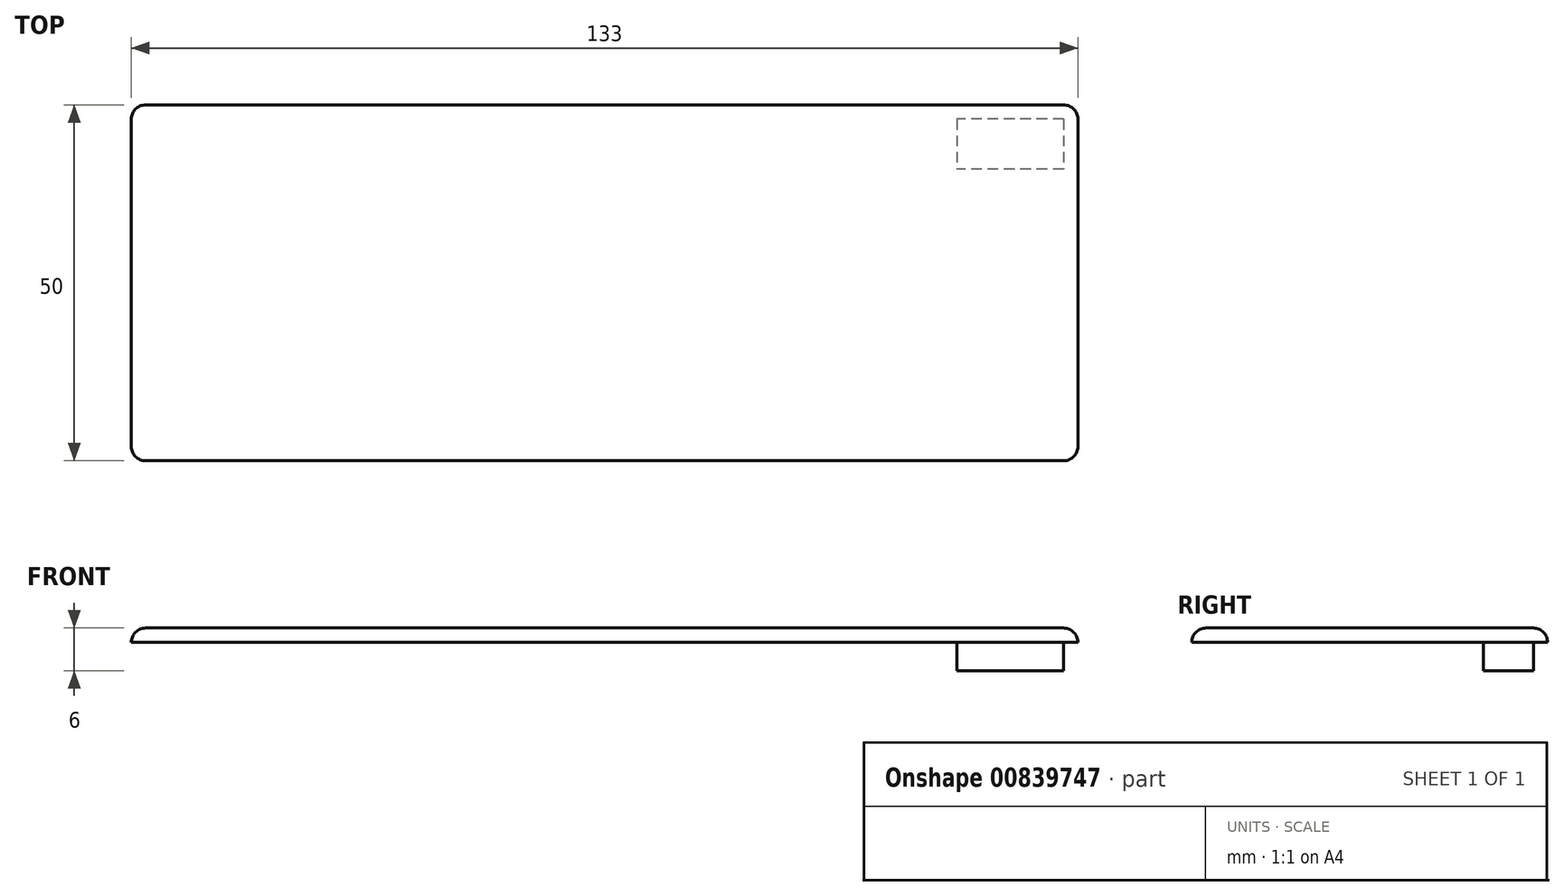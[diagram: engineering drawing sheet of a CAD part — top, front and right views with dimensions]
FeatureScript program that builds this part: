
annotation { "Feature Type Name" : "Feature", "Feature Type Description" : "" }
export const myFeature = defineFeature(function(context is Context, id is Id, definition is map)
    precondition{}
    {
        {
            var Q0;
            Q0=qCreatedBy(makeId("Top.planeOp"),FACE);
            var sketch = newSketch(context, id + "F0", { "sketchPlane" : qUnion([Q0])});
            skLineSegment(sketch, "E0.bottom", {"start": v(66.5, 25) * mm, "end": v(-66.5, 25) * mm});
            skLineSegment(sketch, "E0.top", {"start": v(66.5, -25) * mm, "end": v(-66.5, -25) * mm});
            skLineSegment(sketch, "E0.left", {"start": v(66.5, 25) * mm, "end": v(66.5, -25) * mm});
            skLineSegment(sketch, "E0.right", {"start": v(-66.5, 25) * mm, "end": v(-66.5, -25) * mm});
            skPoint(sketch, "E0.middle", {"position": v(0, 0) * mm});
            skSolve(sketch);
        }
        {
            var Q0;
            Q0=makeQuery(id+"F0.imprint","IMPRINT",FACE,{"disambiguationData":[TD([[makeQuery(id+"F0.imprint","IMPRINT",EDGE,{"derivedFrom":sQuery(id+"F0.wireOp",EDGE,"E0.bottom")}),1.0]])]});
            extrude(context, id + "F1", {"entities" : qUnion([Q0]), "depth" : 2 * mm, "offsetDistance" : 25 * mm});
        }
        {
            var Q0;
            Q0=makeQuery(id+"F1.opExtrude","CAP_FACE",FACE,{"disambiguationData":[OSD([sQuery(id+"F0.wireOp",EDGE,"E0.bottom"),sQuery(id+"F0.wireOp",EDGE,"E0.top"),sQuery(id+"F0.wireOp",EDGE,"E0.left"),sQuery(id+"F0.wireOp",EDGE,"E0.right")])],"isStart":true});
            var sketch = newSketch(context, id + "F2", { "sketchPlane" : qUnion([Q0])});
            skLineSegment(sketch, "E1.bottom", {"start": v(64.5, -23) * mm, "end": v(49.5, -23) * mm});
            skLineSegment(sketch, "E1.top", {"start": v(64.5, -16) * mm, "end": v(49.5, -16) * mm});
            skLineSegment(sketch, "E1.left", {"start": v(64.5, -23) * mm, "end": v(64.5, -16) * mm});
            skLineSegment(sketch, "E1.right", {"start": v(49.5, -23) * mm, "end": v(49.5, -16) * mm});
            skSolve(sketch);
        }
        {
            var Q0;
            Q0 = qSketchRegion(id + "F2", true);
            extrude(context, id + "F3", {"entities" : qUnion([Q0]), "operationType" : NewBodyOperationType.ADD, "depth" : 4 * mm, "offsetDistance" : 25 * mm});
        }
        {
            var Q0;
            Q0=makeQuery(id+"F1.opExtrude","SWEPT_EDGE",EDGE,{"disambiguationData":[OSD([sQuery(id+"F0.wireOp",EDGE,"E0.bottom"),sQuery(id+"F0.wireOp",EDGE,"E0.left")])]});
            var Q1;
            Q1=makeQuery(id+"F1.opExtrude","SWEPT_EDGE",EDGE,{"disambiguationData":[OSD([sQuery(id+"F0.wireOp",EDGE,"E0.top"),sQuery(id+"F0.wireOp",EDGE,"E0.left")])]});
            var Q2;
            Q2=makeQuery(id+"F1.opExtrude","SWEPT_EDGE",EDGE,{"disambiguationData":[OSD([sQuery(id+"F0.wireOp",EDGE,"E0.bottom"),sQuery(id+"F0.wireOp",EDGE,"E0.right")])]});
            var Q3;
            Q3=makeQuery(id+"F1.opExtrude","SWEPT_EDGE",EDGE,{"disambiguationData":[OSD([sQuery(id+"F0.wireOp",EDGE,"E0.top"),sQuery(id+"F0.wireOp",EDGE,"E0.right")])]});
            var Q4;
            Q4=makeQuery(id+"F1.opExtrude","CAP_FACE",FACE,{"disambiguationData":[OSD([sQuery(id+"F0.wireOp",EDGE,"E0.bottom"),sQuery(id+"F0.wireOp",EDGE,"E0.top"),sQuery(id+"F0.wireOp",EDGE,"E0.left"),sQuery(id+"F0.wireOp",EDGE,"E0.right")])],"isStart":false});
            fillet(context, id + "F4", {"entities" : qUnion([Q0, Q1, Q2, Q3, Q4]), "radius" : 2 * mm, "tangentPropagation" : true, "allowEdgeOverflow" : false});
        }
    });
